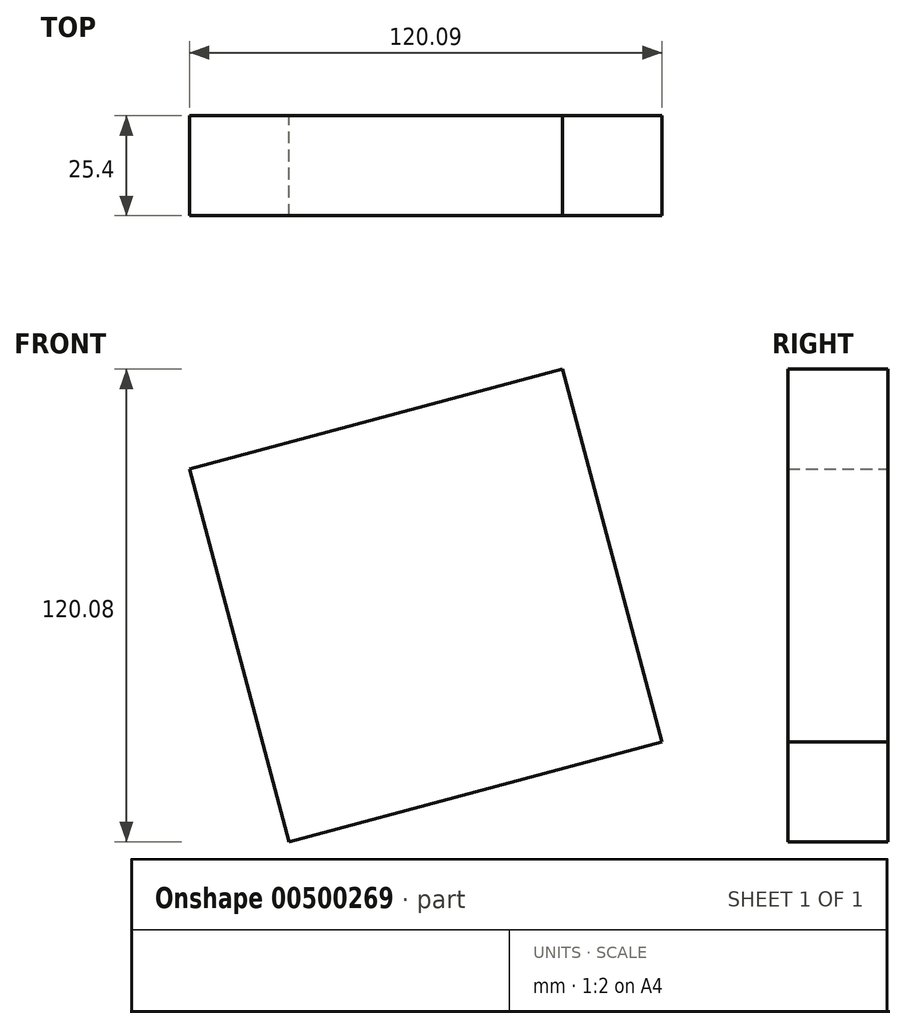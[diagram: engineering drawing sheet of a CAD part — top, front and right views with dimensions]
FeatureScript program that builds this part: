
annotation { "Feature Type Name" : "Feature", "Feature Type Description" : "" }
export const myFeature = defineFeature(function(context is Context, id is Id, definition is map)
    precondition{}
    {
        {
            var Q0;
            Q0=qCreatedBy(makeId("Front.planeOp"),FACE);
            var sketch = newSketch(context, id + "F0", { "sketchPlane" : qUnion([Q0])});
            skCircle(sketch, "E0.cCircle", {"center": v(-5.54, 6.85) * mm, "radius": 69.34 * mm, "construction": true});
            skLineSegment(sketch, "E0.0", {"start": v(29.15, 66.9) * mm, "end": v(54.5, -27.84) * mm});
            skLineSegment(sketch, "E0.1", {"start": v(54.5, -27.84) * mm, "end": v(-40.22, -53.2) * mm});
            skLineSegment(sketch, "E0.2", {"start": v(-40.22, -53.2) * mm, "end": v(-65.58, 41.54) * mm});
            skLineSegment(sketch, "E0.3", {"start": v(-65.58, 41.54) * mm, "end": v(29.15, 66.9) * mm});
            skSolve(sketch);
        }
        {
            var Q0;
            Q0=makeQuery(id+"F0.imprint","IMPRINT",FACE,{"disambiguationData":[TD([[makeQuery(id+"F0.imprint","IMPRINT",EDGE,{"derivedFrom":sQuery(id+"F0.wireOp",EDGE,"E0.0")}),-1.0]])]});
            extrude(context, id + "F1", {"entities" : qUnion([Q0]), "depth" : 25.4 * mm});
        }
    });
